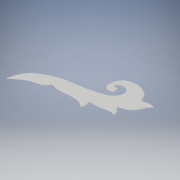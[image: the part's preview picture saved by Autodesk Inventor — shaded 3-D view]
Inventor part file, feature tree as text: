
AUTODESK INVENTOR PART (.ipt)
format: ipt  version: 2019 (Build 230136000, 136)  size: 651,264 bytes
history: native  units: mm
features: fillet x22, plane x2, sketch x2, extrude x2
ambient origin geometry x8: Origin, YZ Plane, XZ Plane, XY Plane, X Axis, Y Axis, Z Axis, Center Point
bodies: Body1 (feature_tree)
feature tree (28):
  plane  "Work Plane6"
  sketch  "Sketch5"  dims[d2=2000.0mm d3=0.0mm d5=2000.0mm d6=200.0mm d7=2000.0mm d8=800.0mm d9=300.0mm d10=2000.0mm d11=2000.0mm d12=2000.0mm d13=2000.0mm d14=2000.0mm d15=3000.0mm d16=1000.0mm d17=700.0mm d18=1000.0mm d19=299.0mm d20=700.0mm d21=2000.0mm d22=2000.0mm d23=500.0mm d24=500.0mm d25=1800.0mm d26=0.0mm]
  plane  "Work Plane7"
  extrude  "Extrusion2"  Depth=2000.0mm
  fillet  "Fillet2"  Radius=200.0mm
  fillet  "Fillet3"  Radius=2000.0mm
  fillet  "Fillet4"  Radius=800.0mm
  fillet  "Fillet5"  Radius=300.0mm
  fillet  "Fillet6"  Radius=2000.0mm
  fillet  "Fillet7"  Radius=2000.0mm
  fillet  "Fillet8"  Radius=2000.0mm
  fillet  "Fillet9"  Radius=2000.0mm
  fillet  "Fillet10"  Radius=2000.0mm
  fillet  "Fillet11"  Radius=3000.0mm
  fillet  "Fillet12"  Radius=1000.0mm
  fillet  "Fillet13"  Radius=700.0mm
  fillet  "Fillet14"  Radius=1000.0mm
  fillet  "Fillet15"  Radius=299.0mm
  fillet  "Fillet16"  Radius=700.0mm
  fillet  "Fillet17"  Radius=2000.0mm
  fillet  "Fillet18"  Radius=2000.0mm
  fillet  "Fillet19"  Radius=500.0mm
  fillet  "Fillet20"  Radius=500.0mm
  fillet  "Fillet21"  Radius=1800.0mm
  extrude  "Extrusion3"  Depth=200.0mm
  fillet  "Fillet22"  [1 undecoded]
  fillet  "Fillet23"  [1 undecoded]
  sketch  "Sketch8"  dims[d27=300.0mm d28=200.0mm]
note: 2 required parameter values undecoded (feature->parameter linkage not recoverable at this tier; creation-order binding heuristic only, values carry confidence <= 0.55)
